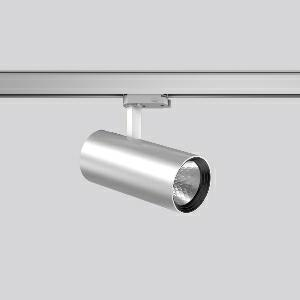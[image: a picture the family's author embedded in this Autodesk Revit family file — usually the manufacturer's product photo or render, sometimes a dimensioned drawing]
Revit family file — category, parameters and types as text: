
# Revit family: deecos_s_mini_742193_004_a806
name_source: partatom
category: Lighting Fixtures
units: mm (PartAtom-declared; Revit-internal decimal feet)

## family parameters
Cut with Voids When Loaded = No
Host = Face
Light Source = No
Part Type = Normal
Room Calculation Point = No
Round Connector Dimension = Use Diameter
Shared = No

## types (1)
- DEECOS S mini (1 x LED Modul 930, 2200 lm, 3000)
    Apparent Load = 22 VA
    Approval mark = CE
    CIE Flux Codes = 100 100 100 100 100
    Color Rendering = 90
    Color Temperature = 3000
    Default Elevation = 1800 mm
    Description = Series: DEECOS S mini
LED surface-mounted projector in modern design with no visible cooling ribs. Housing: die-cast aluminium, powder-coated. Rotation range: 356°. Swivel range: 90°. Black plastic ring and recessed LED to prevent glare from the side. Optical assembly with reflector made of MIRO-Silver with 98% total light reflection for outstanding efficiency - can be changed without tools. Best colour rendering index Ra>90. Superspot version with small spot LED. With multi adaptor for 3-circuit tracks 230 V. Suitable for Track on ceiling, Wall track. High quality converter without flickering and stroboscopic effect. The following accessories can be mounted without use of tools: interchangeable lenses, decorative glasses, honeycomb louvre, clear and frosted diffusers, white interchangeable plastic ring. 
Colour: silver
Diameter: 87 mm
Height: 214 mm
Lamp: LED
Socket: without socket
Colour temperature: 3000K
Colour rendering index (CRI): 92
System power: 22 W
Rated luminous flux: 2200 lm
Luminous efficiency: 100 lm/W
Control gear: Regulated power supply
Protection class: I
Type of protection: IP 20
    Height = 214 mm
    Lamp = 1 x LED Modul 930
    Lamp Light Flux = 2200 lm
    Lamp count = 1
    Length = 87 mm
    Lifetime = 50000 h
    Luminous efficacy = 100 lm/W
    Manufacturer = RZB
    ModVariant = No
    Model = 742193.004
    Mounting Place = Ceiling
    Mounting Type = Rail mounted
    Number of Poles = 1
    OnlyDefault = Yes
    Power Factor = 1
    Product Name = DEECOS S mini
    Product group = Track mounted projectors
    ProductGroupID = 301
    Protection Class = Protection class I
    Protection Degree = IP 20
    RLX_Detail_Level = 1
    RLX_Emergency_Light_Flux = 0 lm
    RLX_Emergency_Type = 0
    RLX_Emergency_Type_DB = No
    RlxData = <blob elided: 37309 chars, md5=129bc48d>
    Socket = socket
    Standby Power = 0 W
    System Light Flux = 2200 lm
    System Power = 22 W
    Type Comments = Product without accessories
    Type Image = 741926.004.jpg
    URL = http://relux.com
    VarID = ---
    Voltage = 230 V
    Voltage Range = 220-240 V
    Weight = 0.00 kg
    Width = 0 mm  [stored 0 ft]

note: [stored X ft] marks values corroborated as IEEE doubles in the binary element streams (Revit-internal decimal feet)

## geometry (parser evidence)
native form markers: Blend x4, Sweep x11
no freeform markers — native parametric forms only
